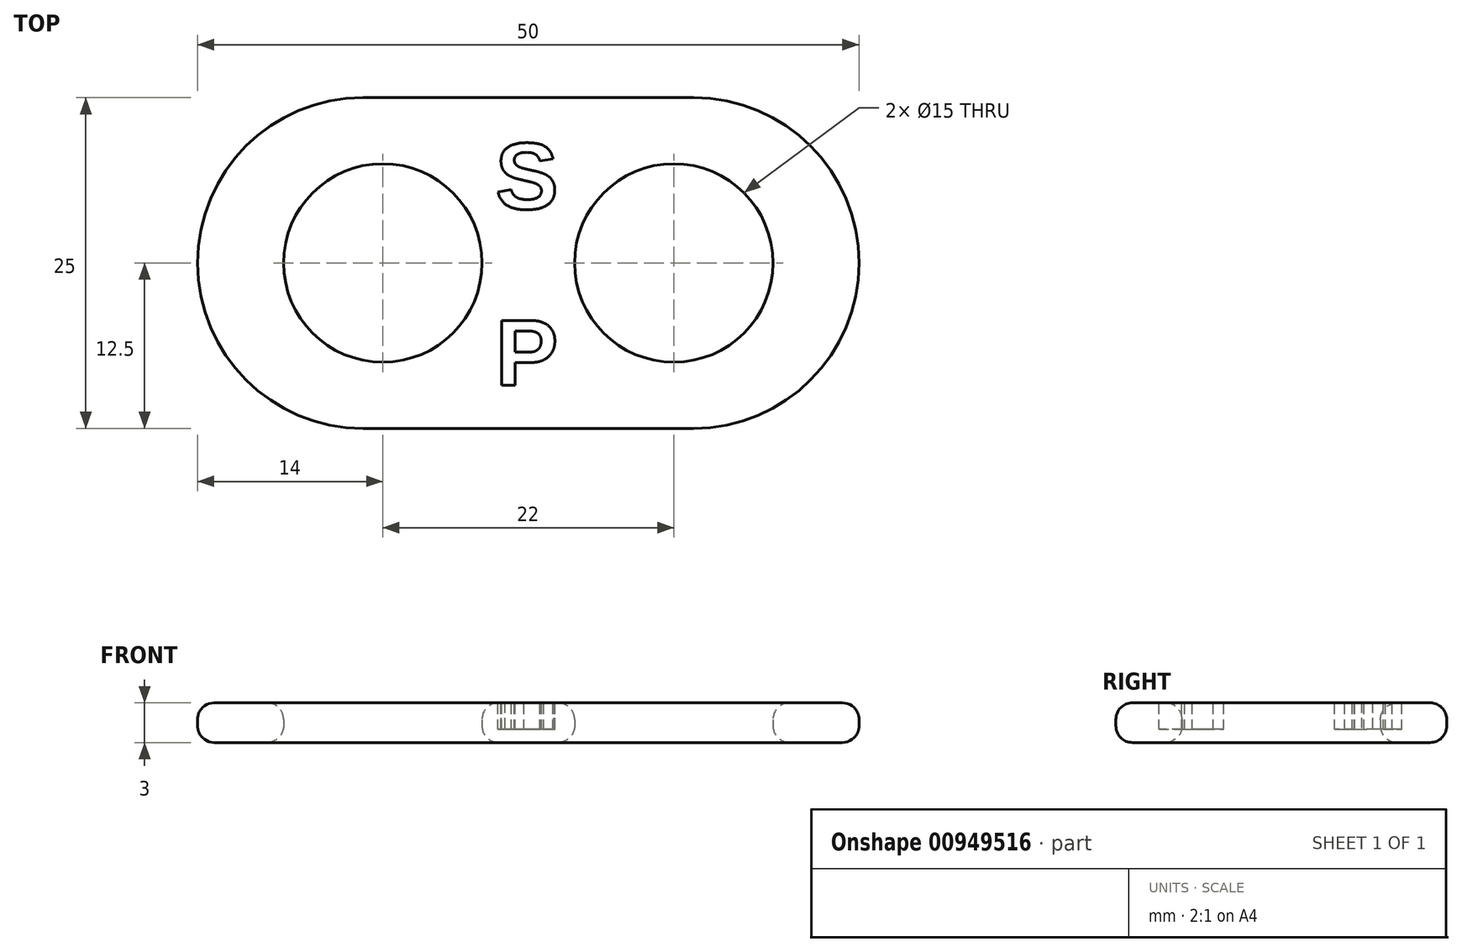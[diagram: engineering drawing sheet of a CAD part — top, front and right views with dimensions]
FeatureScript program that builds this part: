
annotation { "Feature Type Name" : "Feature", "Feature Type Description" : "" }
export const myFeature = defineFeature(function(context is Context, id is Id, definition is map)
    precondition{}
    {
        {
            var Q0;
            Q0=qCreatedBy(makeId("Top.planeOp"),FACE);
            var sketch = newSketch(context, id + "F0", { "sketchPlane" : qUnion([Q0])});
            skLineSegment(sketch, "E0.bottom", {"start": v(-12.5, 12.5) * mm, "end": v(12.5, 12.5) * mm});
            skLineSegment(sketch, "E0.top", {"start": v(-12.5, -12.5) * mm, "end": v(12.5, -12.5) * mm});
            skLineSegment(sketch, "E0.left", {"start": v(-25, 0) * mm, "end": v(-25, 0) * mm});
            skLineSegment(sketch, "E0.right", {"start": v(25, 0) * mm, "end": v(25, 0) * mm});
            skCircle(sketch, "E1", {"center": v(-11, 0) * mm, "radius": 7.5 * mm});
            skCircle(sketch, "E2", {"center": v(11, 0) * mm, "radius": 7.5 * mm});
            skPoint(sketch, "E3.visualSharp", {"position": v(-25, 12.5) * mm});
            skArc(sketch, "E3.filletArc", {"start": v(-12.5, 12.5) * mm, "mid": v(-21.34, 8.84) * mm, "end": v(-25, 0) * mm});
            skPoint(sketch, "E4.visualSharp", {"position": v(-25, -12.5) * mm});
            skArc(sketch, "E4.filletArc", {"start": v(-25, 0) * mm, "mid": v(-21.34, -8.84) * mm, "end": v(-12.5, -12.5) * mm});
            skPoint(sketch, "E5.visualSharp", {"position": v(25, 12.5) * mm});
            skArc(sketch, "E5.filletArc", {"start": v(25, 0) * mm, "mid": v(21.34, 8.84) * mm, "end": v(12.5, 12.5) * mm});
            skPoint(sketch, "E6.visualSharp", {"position": v(25, -12.5) * mm});
            skArc(sketch, "E6.filletArc", {"start": v(12.5, -12.5) * mm, "mid": v(21.34, -8.84) * mm, "end": v(25, 0) * mm});
            skSolve(sketch);
        }
        {
            var Q0;
            Q0=makeQuery(id+"F0.imprint","IMPRINT",FACE,{"disambiguationData":[TD([[makeQuery(id+"F0.imprint","IMPRINT",EDGE,{"derivedFrom":sQuery(id+"F0.wireOp",EDGE,"E0.bottom")}),-1.0]])]});
            extrude(context, id + "F1", {"entities" : qUnion([Q0]), "depth" : 3 * mm, "offsetDistance" : 25 * mm});
        }
        {
            var Q0;
            Q0=makeQuery(id+"F1.opExtrude","CAP_EDGE",EDGE,{"disambiguationData":[OSD([sQuery(id+"F0.wireOp",EDGE,"E1")])],"isStart":false});
            var Q1;
            Q1=makeQuery(id+"F1.opExtrude","CAP_EDGE",EDGE,{"disambiguationData":[OSD([sQuery(id+"F0.wireOp",EDGE,"E2")])],"isStart":false});
            var Q2;
            Q2=makeQuery(id+"F1.opExtrude","CAP_EDGE",EDGE,{"disambiguationData":[OSD([sQuery(id+"F0.wireOp",EDGE,"E0.bottom")])],"isStart":true});
            var Q3;
            Q3=makeQuery(id+"F1.opExtrude","CAP_EDGE",EDGE,{"disambiguationData":[OSD([sQuery(id+"F0.wireOp",EDGE,"E3.filletArc"),sQuery(id+"F0.wireOp",EDGE,"E4.filletArc")])],"isStart":false});
            var Q4;
            Q4=makeQuery(id+"F1.opExtrude","CAP_EDGE",EDGE,{"disambiguationData":[OSD([sQuery(id+"F0.wireOp",EDGE,"E1")])],"isStart":true});
            var Q5;
            Q5=makeQuery(id+"F1.opExtrude","CAP_EDGE",EDGE,{"disambiguationData":[OSD([sQuery(id+"F0.wireOp",EDGE,"E2")])],"isStart":true});
            fillet(context, id + "F2", {"entities" : qUnion([Q0, Q1, Q2, Q3, Q4, Q5]), "radius" : 1.25 * mm, "tangentPropagation" : true, "allowEdgeOverflow" : false});
        }
        {
            var Q0;
            Q0=makeQuery(id+"F1.opExtrude","CAP_FACE",FACE,{"disambiguationData":[OSD([sQuery(id+"F0.wireOp",EDGE,"E0.bottom"),sQuery(id+"F0.wireOp",EDGE,"E0.top"),sQuery(id+"F0.wireOp",EDGE,"E1"),sQuery(id+"F0.wireOp",EDGE,"E2"),sQuery(id+"F0.wireOp",EDGE,"E3.filletArc"),sQuery(id+"F0.wireOp",EDGE,"E4.filletArc"),sQuery(id+"F0.wireOp",EDGE,"E5.filletArc"),sQuery(id+"F0.wireOp",EDGE,"E6.filletArc")])],"isStart":false});
            var sketch = newSketch(context, id + "F3", { "sketchPlane" : qUnion([Q0])});
            skText(sketch, "E7", { "text": "S", "fontName": "Arimo-Bold.ttf"});
            skText(sketch, "E8", { "text": "P", "fontName": "Arimo-Bold.ttf"});
            const initialGuessF3  = {"E7": [-0.0025, 0.00409, 1, 0, 0.00516], "E8": [-0.0025, -0.00925, 1, 0, 0.00513]};
            skSetInitialGuess(sketch, initialGuessF3);
            skSolve(sketch);
        }
        {
            var Q0;
            Q0 = qSketchRegion(id + "F3", true);
            extrude(context, id + "F4", {"entities" : qUnion([Q0]), "operationType" : NewBodyOperationType.REMOVE, "oppositeDirection" : true, "depth" : 2 * mm, "offsetDistance" : 25 * mm});
        }
    });
